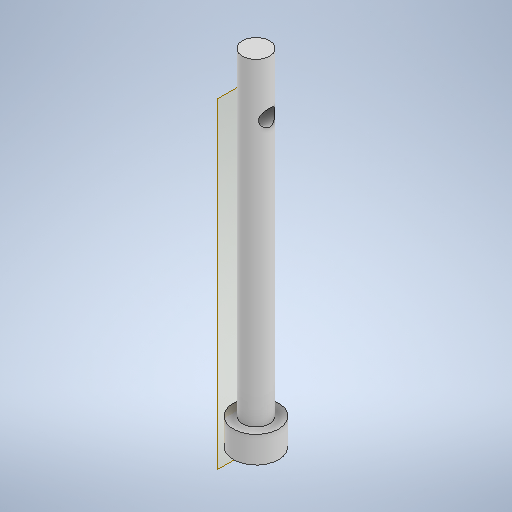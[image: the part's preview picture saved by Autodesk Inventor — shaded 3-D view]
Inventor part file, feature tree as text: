
AUTODESK INVENTOR PART (.ipt)
format: ipt  version: 2025.2 (Build 292293000, 293)  size: 254,464 bytes
history: native  units: mm
features: sketch x4, extrude x3, other x2
ambient origin geometry x8: Origin, YZ Plane, XZ Plane, XY Plane, X Axis, Y Axis, Z Axis, Center Point
bodies: Body1 (feature_tree)
feature tree (9):
  other  "Bryła1"
  extrude  "Wyciągnięcie proste1"  Depth=8.5mm
  extrude  "Wyciągnięcie proste2"  Depth=5.0mm TaperAngle=0.0deg
  other  "Płaszczyzna konstrukcyjna1"
  sketch  "Szkic3"
  extrude  "Wyciągnięcie proste3"  Depth=5.1mm
  sketch  "Szkic1"
  sketch  "Szkic2"
  sketch  "Szkic4"
